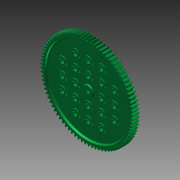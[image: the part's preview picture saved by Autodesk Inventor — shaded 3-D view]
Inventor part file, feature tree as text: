
AUTODESK INVENTOR PART (.ipt)
format: ipt  version: 2014 SP1 (Build 180222100, 222)  size: 946,688 bytes
history: native  units: in
note: dims shown in document units (in); Inventor stores cm internally (conversion verified against a paired STEP export)
features: other x1, imported_body x1, extrude x1, sketch x1
ambient origin geometry x8: Origin, YZ Plane, XZ Plane, XY Plane, X Axis, Y Axis, Z Axis, Center Point
bodies: Body1 (feature_tree)
feature tree (4):
  parser-record x1  (decoder bookkeeping rows leaked as tree rows — omitted from the tree; the rows remain in map.json)
  imported_body  "Base1"
  extrude  "Extrusion1"  [1 undecoded]
  sketch  "Sketch1"  dims[d0=1.0in d1=0.0in]
note: 1 required parameter value undecoded (feature->parameter linkage not recoverable at this tier; creation-order binding heuristic only, values carry confidence <= 0.55)
